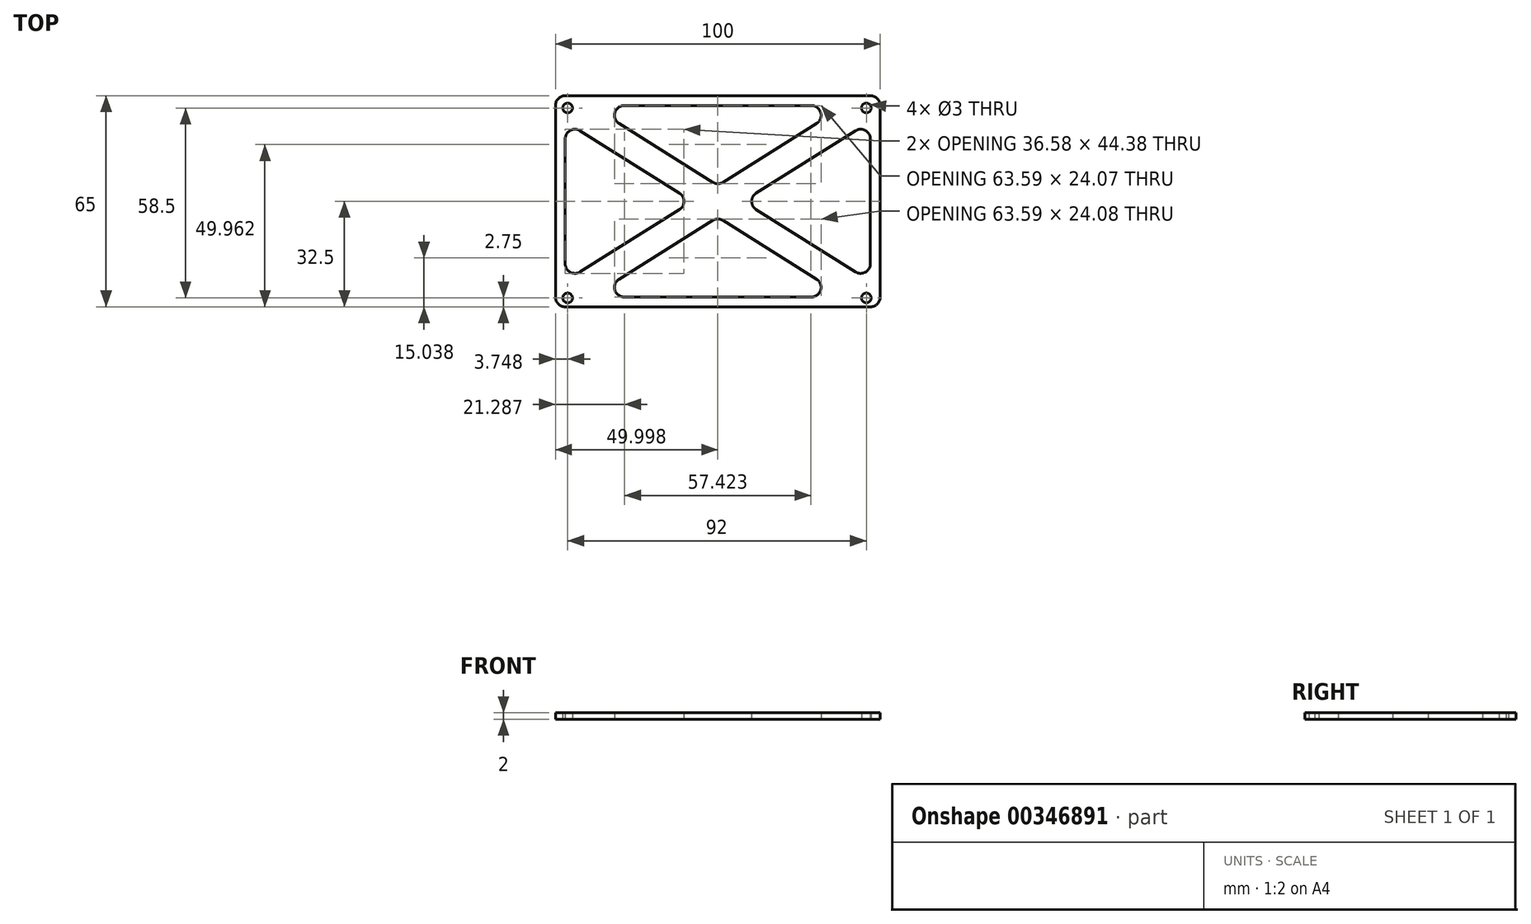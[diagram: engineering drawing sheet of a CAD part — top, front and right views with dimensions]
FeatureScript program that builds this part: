
annotation { "Feature Type Name" : "Feature", "Feature Type Description" : "" }
export const myFeature = defineFeature(function(context is Context, id is Id, definition is map)
    precondition{}
    {
        {
            var Q0;
            Q0=qCreatedBy(makeId("Top.planeOp"),FACE);
            var sketch = newSketch(context, id + "F0", { "sketchPlane" : qUnion([Q0])});
            skCircle(sketch, "E0", {"center": v(-51.9, 0) * mm, "radius": 1.5 * mm});
            skCircle(sketch, "E1", {"center": v(40.1, 0) * mm, "radius": 1.5 * mm});
            skCircle(sketch, "E2", {"center": v(-51.9, -58.5) * mm, "radius": 1.5 * mm});
            skCircle(sketch, "E3", {"center": v(40.1, -58.5) * mm, "radius": 1.5 * mm});
            skLineSegment(sketch, "E4", {"start": v(-52.65, 3.75) * mm, "end": v(-49.65, 3.75) * mm});
            skLineSegment(sketch, "E5", {"start": v(44.35, 0.75) * mm, "end": v(44.35, -2.25) * mm});
            skLineSegment(sketch, "E6", {"start": v(41.35, -61.25) * mm, "end": v(38.35, -61.25) * mm});
            skLineSegment(sketch, "E7", {"start": v(-55.65, -58.25) * mm, "end": v(-55.65, -55.25) * mm});
            skPoint(sketch, "E8.visualSharp", {"position": v(-55.65, 3.75) * mm});
            skArc(sketch, "E8.filletArc", {"start": v(-52.65, 3.75) * mm, "mid": v(-54.77, 2.87) * mm, "end": v(-55.65, 0.75) * mm});
            skPoint(sketch, "E9.visualSharp", {"position": v(44.35, 3.75) * mm});
            skArc(sketch, "E9.filletArc", {"start": v(44.35, 0.75) * mm, "mid": v(43.47, 2.87) * mm, "end": v(41.35, 3.75) * mm});
            skPoint(sketch, "E10.visualSharp", {"position": v(44.35, -61.25) * mm});
            skArc(sketch, "E10.filletArc", {"start": v(41.35, -61.25) * mm, "mid": v(43.47, -60.37) * mm, "end": v(44.35, -58.25) * mm});
            skPoint(sketch, "E11.visualSharp", {"position": v(-55.65, -61.25) * mm});
            skArc(sketch, "E11.filletArc", {"start": v(-55.65, -58.25) * mm, "mid": v(-54.77, -60.37) * mm, "end": v(-52.65, -61.25) * mm});
            skLineSegment(sketch, "E12", {"start": v(-36.04, -4.8) * mm, "end": v(-7.25, -22.87) * mm});
            skLineSegment(sketch, "E13", {"start": v(-48.06, -7.02) * mm, "end": v(-17.48, -26.2) * mm});
            skLineSegment(sketch, "E14", {"start": v(-48.06, -50.48) * mm, "end": v(-17.48, -31.3) * mm});
            skLineSegment(sketch, "E15", {"start": v(-36.04, -52.7) * mm, "end": v(-7.25, -34.63) * mm});
            skLineSegment(sketch, "E16.trimOffspring", {"start": v(-4.06, -22.87) * mm, "end": v(24.74, -4.8) * mm});
            skLineSegment(sketch, "E17.trimOffspring", {"start": v(6.18, -31.3) * mm, "end": v(36.75, -50.48) * mm});
            skLineSegment(sketch, "E18.trimOffspring", {"start": v(6.18, -26.2) * mm, "end": v(36.75, -7.02) * mm});
            skLineSegment(sketch, "E19.trimOffspring", {"start": v(-4.06, -34.63) * mm, "end": v(24.74, -52.7) * mm});
            skPoint(sketch, "E20.visualSharp", {"position": v(-13.43, -28.75) * mm});
            skArc(sketch, "E20.filletArc", {"start": v(-17.48, -31.3) * mm, "mid": v(-16.07, -28.75) * mm, "end": v(-17.48, -26.2) * mm});
            skPoint(sketch, "E21.visualSharp", {"position": v(-5.65, -33.63) * mm});
            skArc(sketch, "E21.filletArc", {"start": v(-4.06, -34.63) * mm, "mid": v(-5.65, -34.17) * mm, "end": v(-7.25, -34.63) * mm});
            skPoint(sketch, "E22.visualSharp", {"position": v(2.13, -28.75) * mm});
            skArc(sketch, "E22.filletArc", {"start": v(6.18, -26.2) * mm, "mid": v(4.77, -28.75) * mm, "end": v(6.18, -31.3) * mm});
            skPoint(sketch, "E23.visualSharp", {"position": v(-5.65, -23.87) * mm});
            skArc(sketch, "E23.filletArc", {"start": v(-7.25, -22.87) * mm, "mid": v(-5.65, -23.33) * mm, "end": v(-4.06, -22.87) * mm});
            skLineSegment(sketch, "E24.trimOffspring", {"start": v(-55.65, -2.25) * mm, "end": v(-55.65, 0.75) * mm});
            skLineSegment(sketch, "E25.trimOffspring", {"start": v(-49.65, -61.25) * mm, "end": v(-52.65, -61.25) * mm});
            skLineSegment(sketch, "E26.trimOffspring", {"start": v(38.35, 3.75) * mm, "end": v(41.35, 3.75) * mm});
            skLineSegment(sketch, "E27.trimOffspring", {"start": v(44.35, -55.25) * mm, "end": v(44.35, -58.25) * mm});
            skLineSegment(sketch, "E28", {"start": v(-55.65, -55.25) * mm, "end": v(-55.65, -2.25) * mm});
            skLineSegment(sketch, "E29", {"start": v(-49.65, -61.25) * mm, "end": v(38.35, -61.25) * mm});
            skLineSegment(sketch, "E30", {"start": v(44.35, -2.25) * mm, "end": v(44.35, -55.25) * mm});
            skLineSegment(sketch, "E31", {"start": v(38.35, 3.75) * mm, "end": v(-49.65, 3.75) * mm});
            skLineSegment(sketch, "E32", {"start": v(-34.45, 0.75) * mm, "end": v(23.15, 0.75) * mm});
            skLineSegment(sketch, "E33", {"start": v(-34.45, -58.25) * mm, "end": v(23.15, -58.25) * mm});
            skLineSegment(sketch, "E34", {"start": v(41.35, -47.94) * mm, "end": v(41.35, -9.56) * mm});
            skLineSegment(sketch, "E35", {"start": v(-52.65, -47.94) * mm, "end": v(-52.65, -9.56) * mm});
            skPoint(sketch, "E36.visualSharp", {"position": v(-52.65, -4.13) * mm});
            skArc(sketch, "E36.filletArc", {"start": v(-48.06, -7.02) * mm, "mid": v(-51.1, -6.93) * mm, "end": v(-52.65, -9.56) * mm});
            skPoint(sketch, "E37.visualSharp", {"position": v(-44.87, 0.75) * mm});
            skArc(sketch, "E37.filletArc", {"start": v(-34.45, 0.75) * mm, "mid": v(-37.33, -1.42) * mm, "end": v(-36.04, -4.8) * mm});
            skPoint(sketch, "E38.visualSharp", {"position": v(33.57, 0.75) * mm});
            skArc(sketch, "E38.filletArc", {"start": v(24.74, -4.8) * mm, "mid": v(26.03, -1.42) * mm, "end": v(23.15, 0.75) * mm});
            skPoint(sketch, "E39.visualSharp", {"position": v(41.35, -4.13) * mm});
            skArc(sketch, "E39.filletArc", {"start": v(41.35, -9.56) * mm, "mid": v(39.8, -6.93) * mm, "end": v(36.75, -7.02) * mm});
            skPoint(sketch, "E40.visualSharp", {"position": v(41.35, -53.37) * mm});
            skArc(sketch, "E40.filletArc", {"start": v(36.75, -50.48) * mm, "mid": v(39.8, -50.57) * mm, "end": v(41.35, -47.94) * mm});
            skPoint(sketch, "E41.visualSharp", {"position": v(33.57, -58.25) * mm});
            skArc(sketch, "E41.filletArc", {"start": v(23.15, -58.25) * mm, "mid": v(26.03, -56.08) * mm, "end": v(24.74, -52.7) * mm});
            skPoint(sketch, "E42.visualSharp", {"position": v(-44.87, -58.25) * mm});
            skArc(sketch, "E42.filletArc", {"start": v(-36.04, -52.7) * mm, "mid": v(-37.33, -56.08) * mm, "end": v(-34.45, -58.25) * mm});
            skPoint(sketch, "E43.visualSharp", {"position": v(-52.65, -53.37) * mm});
            skArc(sketch, "E43.filletArc", {"start": v(-52.65, -47.94) * mm, "mid": v(-51.1, -50.57) * mm, "end": v(-48.06, -50.48) * mm});
            skSolve(sketch);
        }
        {
            var Q0;
            Q0=qSketchRegion(id+"F0",true);
            extrude(context, id + "F1", {"entities" : qUnion([Q0]), "depth" : 2 * mm});
        }
    });
